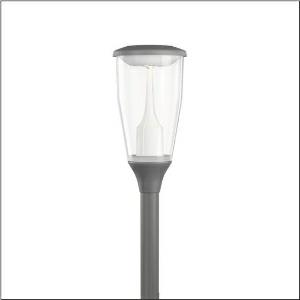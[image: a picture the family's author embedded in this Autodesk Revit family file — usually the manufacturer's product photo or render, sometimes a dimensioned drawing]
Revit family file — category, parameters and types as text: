
# Revit family: dl_11_iq___st1_2a_5xa5575mf14hp00022_5a95
name_source: partatom
category: Lighting Fixtures
units: mm (PartAtom-declared; Revit-internal decimal feet)

## family parameters
Cut with Voids When Loaded = No
Host = Face
Light Source = No
Part Type = Normal
Room Calculation Point = No
Round Connector Dimension = Use Diameter
Shared = No

## types (1)
- --- (1 x LED, 4340 lm, 33.6 W, 2700K)
    Apparent Load = 34 VA
    CIE Flux Codes = 23 60 93 95 100
    Color Rendering = 70
    Color Temperature = 2700K
    Default Elevation = 1800 mm
    Description = DL 11 iQ, mast luminaire, Module 540 iQ-SR, primary light control with 3 zone facetted reflector, of plastic, silver coated, highly specular, structured, primary optical cover: cover, of PMMA, transparent, light distribution: ST1.2a, light emission: direct distribution, primary light characteristic: asymmetric, installation type: post-top, LED, High Power LED, light colour: 727, colour temperature: 2700K, control gear: iQ Street-Remote, control: Street-Remote, Auto-Match, Temp-Guard, Lumen-Switch, Night-Set, Smart-Wire, Light-Fading, Desk-Remote (wireless, voltage-free reading and setting of iQ features in the workshop via application-optimized NFC function/RFID function), optimised constant luminous flux control (CLO 2.0), mains connection: 220..240V, AC, 50/60Hz, connection cable pre-assembled, cable length: 5,5m, wiring characteristics: H07RN-F, 5-core, 1.5mm², start of lifetime: 34W, end of service life: 36W, luminaire housing, upper part, of diecast aluminium, coated, SITECO metallic grey (DB 702S), spigot size: 76mm (post-top), mounting height: 3..5m, post-top mast mounting element, of diecast aluminium, coated, SITECO metallic grey (DB 702S), Module 540 iQ-SR, traffic white (RAL 9016), equipment: Power, protection rating (complete): IP66, insulation class (complete): insulation class II (safety insulation), certification: CE, ENEC, ENEC+, VDE, impact resistance: IK07, packaging unit: 1 piece

Light Distribution: ST1.2a
    Height = 665 mm
    Lamp = 1 x LED
    Lamp Light Flux = 4340 lm
    Lamp Power = 33.6 W
    Lamp count = 1
    Length = 334 mm
    Luminous efficacy = 129 lm/W
    Manufacturer = Siteco
    ModVariant = No
    Model = 5XA5575MF14HP00022
    Number of Poles = 1
    OnlyDefault = Yes
    Power Factor = 1
    Product Name = DL 11 iQ | ST1.2a
    Product group = mast luminaire | pylon top
    ProductGroupID = 6100
    Protection Class = Protection class II
    Protection Degree = IP 66
    RLX_Detail_Level = 1
    RLX_Emergency_Light_Flux = 0 lm
    RLX_Emergency_Type = 0
    RLX_Emergency_Type_DB = No
    RlxData = <blob elided: 155297 chars, md5=7e5dfebd>
    Socket = socket
    Standby Power = 0 W
    System Light Flux = 4340 lm
    System Power = 34 W
    Type Comments = factory setting: luminous flux: 100 % | dim-lin: 254 | 695 mA
    Type Image = l_1258354.jpg
    URL = http://relux.com
    VarID = @adj_040083
    Voltage = 0 V
    Weight = 0.00 kg
    Width = 0 mm  [stored 0 ft]

note: [stored X ft] marks values corroborated as IEEE doubles in the binary element streams (Revit-internal decimal feet)

## geometry (parser evidence)
native form markers: Blend x4, Sweep x9
no freeform markers — native parametric forms only
